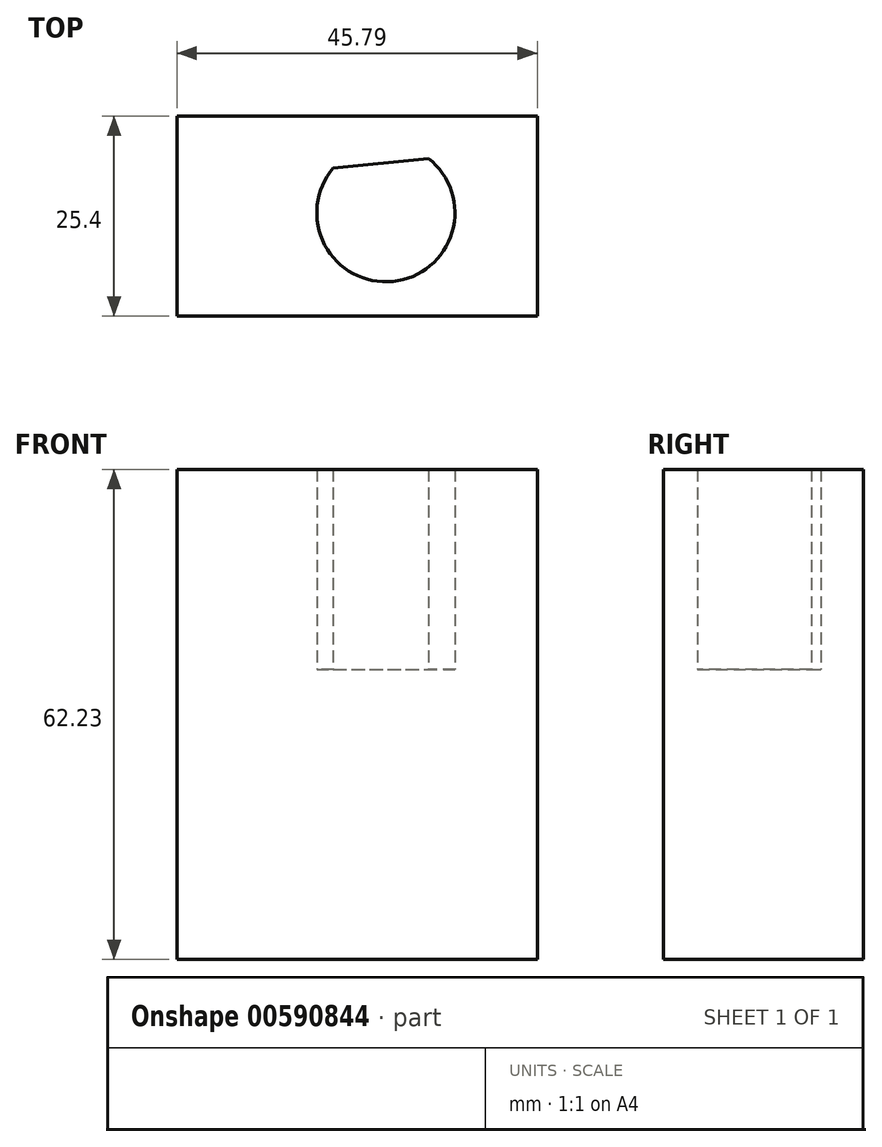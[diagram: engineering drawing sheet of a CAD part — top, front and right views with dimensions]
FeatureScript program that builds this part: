
annotation { "Feature Type Name" : "Feature", "Feature Type Description" : "" }
export const myFeature = defineFeature(function(context is Context, id is Id, definition is map)
    precondition{}
    {
        {
            var Q0;
            Q0=qCreatedBy(makeId("Front.planeOp"),FACE);
            var sketch = newSketch(context, id + "F0", { "sketchPlane" : qUnion([Q0])});
            skLineSegment(sketch, "E0", {"start": v(-29.5, 14.53) * mm, "end": v(-29.5, -22.3) * mm});
            skLineSegment(sketch, "E1", {"start": v(-29.5, -22.3) * mm, "end": v(16.3, -22.3) * mm});
            skLineSegment(sketch, "E2", {"start": v(16.3, -22.3) * mm, "end": v(16.3, 14.53) * mm});
            skLineSegment(sketch, "E3", {"start": v(16.3, 14.53) * mm, "end": v(-29.5, 14.53) * mm});
            skSolve(sketch);
        }
        {
            var Q0;
            Q0=makeQuery(id+"F0.imprint","IMPRINT",FACE,{"disambiguationData":[TD([[makeQuery(id+"F0.imprint","IMPRINT",EDGE,{"derivedFrom":sQuery(id+"F0.wireOp",EDGE,"E0")}),1.0]])]});
            extrude(context, id + "F1", {"entities" : qUnion([Q0]), "depth" : 25.4 * mm, "offsetDistance" : 25.4 * mm});
        }
        {
            var Q0;
            Q0=makeQuery(id+"F1.opExtrude","SWEPT_FACE",FACE,{"disambiguationData":[OSD([sQuery(id+"F0.wireOp",EDGE,"E3")])]});
            var sketch = newSketch(context, id + "F2", { "sketchPlane" : qUnion([Q0])});
            skArc(sketch, "E4", {"start": v(-9.64, -6.6) * mm, "mid": v(-2.08, -21) * mm, "end": v(2.45, -5.38) * mm});
            skLineSegment(sketch, "E5", {"start": v(-9.64, -6.6) * mm, "end": v(2.45, -5.38) * mm});
            skSolve(sketch);
        }
        {
            var Q0;
            Q0=makeQuery(id+"F2.imprint","IMPRINT",FACE,{"disambiguationData":[TD([[makeQuery(id+"F2.imprint","IMPRINT",EDGE,{"derivedFrom":sQuery(id+"F2.wireOp",EDGE,"E4")}),-1.0]])]});
            extrude(context, id + "F3", {"entities" : qUnion([Q0]), "operationType" : NewBodyOperationType.ADD, "depth" : 25.4 * mm, "offsetDistance" : 25.4 * mm});
        }
    });
